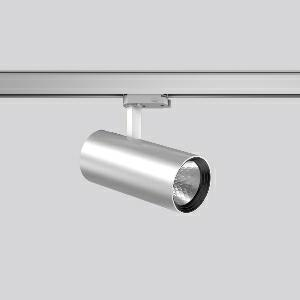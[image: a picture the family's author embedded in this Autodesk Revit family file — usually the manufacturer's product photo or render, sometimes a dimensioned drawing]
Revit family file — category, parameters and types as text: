
# Revit family: deecos_s_mini_742193_004_76_c3c9
name_source: partatom
category: Lighting Fixtures
units: mm (PartAtom-declared; Revit-internal decimal feet)

## family parameters
Cut with Voids When Loaded = No
Host = Face
Light Source = No
Part Type = Normal
Room Calculation Point = No
Round Connector Dimension = Use Diameter
Shared = No

## types (1)
- DEECOS S mini (1 x LED Modul 930, 2200 lm, 3000)
    Apparent Load = 22 VA
    Approval mark = CE
    CIE Flux Codes = 100 100 100 100 100
    Color Rendering = 90
    Color Temperature = 3000
    Default Elevation = 1800 mm
    Description = Series: DEECOS S mini
LED surface-mounted projector in modern design with no visible cooling ribs. Housing: die-cast aluminium, powder-coated. Rotation range: 356°. Swivel range: 90°. Black plastic ring and recessed LED to prevent glare from the side. Optical assembly with reflector made of MIRO-Silver with 98% total light reflection for outstanding efficiency - can be changed without tools. Best colour rendering index Ra>90. Superspot version with small spot LED. With adapter for RZB 3-circuit DALI tracks. Suitable for Track on ceiling, Wall track. High quality converter without flickering and stroboscopic effect. The following accessories can be mounted without use of tools: interchangeable lenses, decorative glasses, honeycomb louvre, clear and frosted diffusers, white interchangeable plastic ring. 
Colour: silver
Diameter: 87 mm
Height: 214 mm
Lamp: LED
Socket: without socket
Colour temperature: 3000K
Colour rendering index (CRI): 92
System power: 22 W
Rated luminous flux: 2200 lm
Luminous efficiency: 100 lm/W
Control gear: Converter, dimmable, DALI
Protection class: I
Type of protection: IP 20
    Height = 214 mm
    Lamp = 1 x LED Modul 930
    Lamp Light Flux = 2200 lm
    Lamp count = 1
    Length = 87 mm
    Lifetime = 50000 h
    Luminous efficacy = 100 lm/W
    Manufacturer = RZB
    ModVariant = No
    Model = 742193.004.76
    Mounting Place = Ceiling
    Mounting Type = Rail mounted
    Number of Poles = 1
    OnlyDefault = Yes
    Power Factor = 1
    Product Name = DEECOS S mini
    Product group = Track mounted projectors
    ProductGroupID = 301
    Protection Class = Protection class I
    Protection Degree = IP 20
    RLX_Detail_Level = 1
    RLX_Emergency_Light_Flux = 0 lm
    RLX_Emergency_Type = 0
    RLX_Emergency_Type_DB = No
    RlxData = <blob elided: 37253 chars, md5=f8f390e8>
    Socket = socket
    Standby Power = 0 W
    System Light Flux = 2200 lm
    System Power = 22 W
    Type Comments = Product without accessories
    Type Image = 741926.004.jpg
    URL = http://relux.com
    VarID = ---
    Voltage = 230 V
    Voltage Range = 220-240 V
    Weight = 0.00 kg
    Width = 0 mm  [stored 0 ft]

note: [stored X ft] marks values corroborated as IEEE doubles in the binary element streams (Revit-internal decimal feet)

## geometry (parser evidence)
native form markers: Blend x4, Sweep x11
no freeform markers — native parametric forms only
